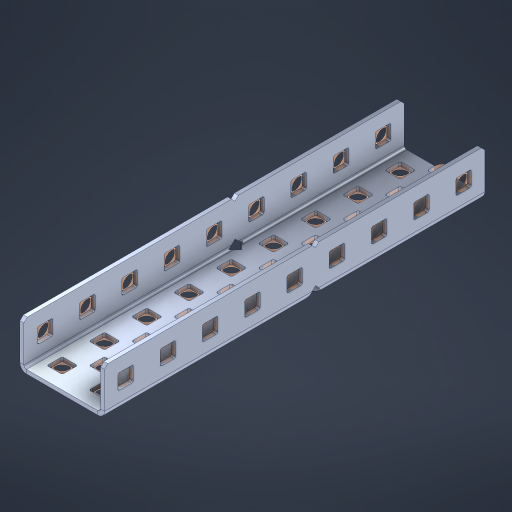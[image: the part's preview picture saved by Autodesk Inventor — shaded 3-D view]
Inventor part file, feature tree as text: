
AUTODESK INVENTOR PART (.ipt)
format: ipt  version: 2023 (Build 270158000, 158)  size: 863,232 bytes
history: native  units: in
note: dims shown in document units (in); Inventor stores cm internally (conversion verified against a paired STEP export)
features: other x52, extrude x43, sheet_metal_op x11, sketch x10, pattern_linear x2, mirror x1, chamfer x1
ambient origin geometry x8: Origin, YZ Plane, XZ Plane, XY Plane, X Axis, Y Axis, Z Axis, Center Point
bodies: Solid1 (feature_tree), Body (feature_tree)
feature tree (120):
  sheet_metal_op  "Flanges"
  other  "Flange Pattern Plane"
  other  "Flange Pattern Sketch"
  sheet_metal_op  "Flange Pattern"
  sheet_metal_op  "Body Pattern"
  pattern_linear  "Center Pattern"  Spacing1=0.0469in  [1 undecoded]
  other  "Arc Length"
  mirror  "Notch Mirror"
  pattern_linear  "Notch Pattern"  Spacing1=0.182in  [1 undecoded]
  chamfer  "End Chamfer"
  extrude  "Half Cut"  Depth=0.02in
  sketch  "Sketch1"  dims[d0=1.0in]
  other  "Plate1"
  sketch  "Sketch2"  dims[d1=4.5in]
  other  "Plate2"
  sheet_metal_op  "Bend1"
  sheet_metal_op  "Corner1"
  sketch  "Sketch3"  dims[d2=0.0469in]
  sketch  "Sketch7"  dims[d3=0.0469in]
  other  "Srf1"
  other  "Srf2"
  sketch  "Sketch8"  dims[d4=0.0234in]
  sketch  "Sketch9"  dims[d5=0.0938in]
  other  "Srf91"
  sheet_metal_op  "Body Pattern Sketch"
  other  "Srf92"
  sketch  "Sketch13"  dims[d6=0.0469in]
  sketch  "Sketch14"  dims[d7=0.5in d8=90.0deg d9=0.0312in]
  sketch  "Sketch15"  dims[d10=0.1875in]
  sketch  "Sketch16"  dims[d11=0.0469in d12=0.0469in d16=0.182in d17=0.02in d18=0.0469in d19=0.0in d20=0.25in d21=0.25in d38=3.5433in d40=0.5in d41=0.7874in d43=1.0in d46=0.172in d47=1.0in d48=0.0in d49=0.182in d50=0.02in d51=0.25in d52=0.25in d53=0.0469in d54=0.0in d55=0.172in d56=1.0in d57=0.0in d58=0.25in d60=3.5433in d62=0.5in d63=0.7874in d65=0.5in d85=0.1227in d86=0.1659in d88=0.04in d89=0.0469in d90=0.0in d91=0.04in d92=0.0491in d95=2.5in d96=0.04in d97=0.25in d98=45.0deg d99=0.25in d100=0.5in d101=0.0in d102=2.497in d106=0.182in d107=0.02in d108=0.5in d109=0.5in d110=0.0469in d111=0.0in d112=0.172in d113=0.5in d114=0.0in d117=0.5in d118=0.5in d119=0.5in]
  other  "Srf786"
  other  "Srf823"
  other  "Srf824"
  other  "Srf825"
  other  "Srf826"
  other  "Srf827"
  other  "Srf828"
  other  "Srf829"
  other  "Srf856"
  other  "Srf857"
  other  "Srf858"
  other  "Srf859"
  other  "Srf860"
  other  "Srf861"
  other  "Srf862"
  other  "Srf889"
  other  "Srf890"
  other  "Srf891"
  other  "Srf892"
  other  "Srf893"
  other  "Srf894"
  other  "Srf895"
  other  "Srf896"
  other  "Srf922"
  other  "Srf923"
  other  "Srf924"
  other  "Srf925"
  other  "Srf926"
  other  "Srf959"
  other  "Srf960"
  other  "Srf961"
  other  "Srf962"
  other  "Srf963"
  other  "Srf1143"
  other  "Srf1144"
  other  "Srf1145"
  other  "Srf1146"
  other  "Srf1199"
  other  "Srf1200"
  other  "Srf1201"
  other  "Srf1202"
  sheet_metal_op  "Flange Stamp"
  sheet_metal_op  "Flange Circle"
  sheet_metal_op  "Body Stamp"
  sheet_metal_op  "Body Circle"
  other  "Center Stamp"
  other  "Center Circle"
  sheet_metal_op  "Notch"
  extrude  "ExtrusionSrf2"  Depth=0.0469in
  extrude  "ExtrusionSrf92"  TaperAngle=0.0deg  [1 undecoded]
  extrude  "ExtrusionSrf823"  Depth=0.5in
  extrude  "ExtrusionSrf824"  Depth=0.5in
  extrude  "ExtrusionSrf825"  Depth=0.5in
  extrude  "ExtrusionSrf826"  Depth=0.5in
  extrude  "ExtrusionSrf827"  Depth=1.0in TaperAngle=0.0deg
  extrude  "ExtrusionSrf828"  Depth=0.5in
  extrude  "ExtrusionSrf829"  Depth=0.02in
  extrude  "ExtrusionSrf856"  Depth=0.5in
  extrude  "ExtrusionSrf857"  Depth=0.5in
  extrude  "ExtrusionSrf858"  Depth=0.0469in
  extrude  "ExtrusionSrf859"  TaperAngle=0.0deg  [1 undecoded]
  extrude  "ExtrusionSrf860"  Depth=0.5in
  extrude  "ExtrusionSrf861"  Depth=1.0in TaperAngle=0.0deg
  extrude  "ExtrusionSrf862"  Depth=0.5in
  extrude  "ExtrusionSrf889"  Depth=0.5in
  extrude  "ExtrusionSrf890"  Depth=0.5in
  extrude  "ExtrusionSrf891"  Depth=0.5in
  extrude  "ExtrusionSrf892"  Depth=0.5in
  extrude  "ExtrusionSrf893"  Depth=0.5in
  extrude  "ExtrusionSrf894"  Depth=0.0469in
  extrude  "ExtrusionSrf895"  TaperAngle=0.0deg  [1 undecoded]
  extrude  "ExtrusionSrf896"  Depth=0.5in
  extrude  "ExtrusionSrf922"  Depth=0.5in
  extrude  "ExtrusionSrf923"  Depth=2.5in
  extrude  "ExtrusionSrf924"  Depth=0.5in TaperAngle=45.0deg
  extrude  "ExtrusionSrf925"  Depth=0.5in
  extrude  "ExtrusionSrf926"  Depth=0.5in TaperAngle=0.0deg
  extrude  "ExtrusionSrf959"  Depth=0.5in
  extrude  "ExtrusionSrf960"  Depth=0.5in
  extrude  "ExtrusionSrf961"  Depth=0.02in
  extrude  "ExtrusionSrf962"  Depth=0.5in
  extrude  "ExtrusionSrf963"  Depth=0.5in
  extrude  "ExtrusionSrf1143"  Depth=0.0469in
  extrude  "ExtrusionSrf1144"  TaperAngle=0.0deg  [1 undecoded]
  extrude  "ExtrusionSrf1145"  Depth=0.5in
  extrude  "ExtrusionSrf1146"  Depth=0.5in TaperAngle=0.0deg
  extrude  "ExtrusionSrf1199"  Depth=0.5in
  extrude  "ExtrusionSrf1200"  Depth=0.5in
  extrude  "ExtrusionSrf1201"  Depth=0.5in
  extrude  "ExtrusionSrf1202"  [1 undecoded]
note: 7 required parameter values undecoded (feature->parameter linkage not recoverable at this tier; creation-order binding heuristic only, values carry confidence <= 0.55)
